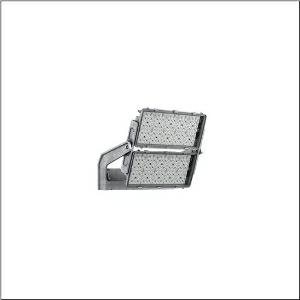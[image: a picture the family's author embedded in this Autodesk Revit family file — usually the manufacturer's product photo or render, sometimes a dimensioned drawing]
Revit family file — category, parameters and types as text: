
# Revit family: floodlight_fl_11_maxi___rs12_5xa779218m01aa_9f10
name_source: partatom
category: Lighting Fixtures
units: mm (PartAtom-declared; Revit-internal decimal feet)

## family parameters
Cut with Voids When Loaded = No
Host = Face
Light Source = No
Part Type = Normal
Room Calculation Point = No
Round Connector Dimension = Use Diameter
Shared = No

## types (1)
- --- (1 x LED, 107970 lm, 941.9 W, 5700K)
    Apparent Load = 942 VA
    CIE Flux Codes = 79 92 99 100 100
    Color Rendering = 80
    Color Temperature = 5700K
    Default Elevation = 1800 mm
    Description = Floodlight FL 11  maxi floodlight; light control with lens of PMMA; cover panel of toughened safety glass, transparent; light distribution: RS12, rotationally symmetric direct distribution, LEDcolour temperature: 5700K, rated luminous flux: 107.970lm, colour rendering: CRI > 80, light colour: 857; luminous efficacy: 115lm/W; brightness control: DMX+RDM; with terminal, 6-pole, max. 2.5mm², mains connection: 220..240V/380..400V AC, 50/60Hz, surge voltage resistance: line to ground: 10kV, ECG replaceable separately, LED unit replaceable without ESD environment, dustproof LED module, dimming range 10..100%; 942W floodlight with 2x LED unit of diecast aluminium, uncoated natural; length: 713mm / width: 651mm / height: 338mm; mounting bracket, of diecast aluminium, uncoated, natural, equipment: Power, protection rating (complete): IP66; insulation class (complete): insulation class I (protective earthing); certification: CE; ball protection: ball impact resistant, only for outdoor installations, rated ambient temperature 10°C, permissible operating ambient temperature: -40..+30°C, permissible storage temperature: -40..+85°C; packaging unit: 1 piece

Light Distribution: RS12
    Height = 320 mm
    Lamp = 1 x LED
    Lamp Light Flux = 107970 lm
    Lamp Power = 941.9 W
    Lamp count = 1
    Length = 712 mm
    Luminous efficacy = 115 lm/W
    Manufacturer = Siteco
    ModVariant = No
    Model = 5XA779218M01AA
    Number of Poles = 1
    OnlyDefault = Yes
    Power Factor = 1
    Product Name = Floodlight FL 11 maxi | RS12
    Product group = floodlight | pylon top
    ProductGroupID = 6101
    Protection Class = Protection class I
    Protection Degree = IP 66
    RLX_Detail_Level = 1
    RlxData = <blob elided: 41901 chars, md5=bdd3cbb4>
    Socket = socket
    Standby Power = 0 W
    System Light Flux = 107970 lm
    System Power = 942 W
    Type Comments = factory setting: luminous flux: 100 % | dim-lin: 254 | 975 mA
    Type Image = l_1006932.jpg
    URL = http://relux.com
    VarID = @adj_095607
    Voltage = 0 V
    Weight = 0.00 kg
    Width = 655 mm

## geometry (parser evidence)
native form markers: Blend x4, Sweep x14
no freeform markers — native parametric forms only
